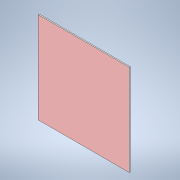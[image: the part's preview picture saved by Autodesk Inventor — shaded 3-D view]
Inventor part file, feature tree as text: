
AUTODESK INVENTOR PART (.ipt)
format: ipt  version: 2022 (Build 260153000, 153)  size: 109,568 bytes
history: native  units: mm
features: extrude x2, sketch x2, other x1
ambient origin geometry x8: Origin, YZ Plane, XZ Plane, XY Plane, X Axis, Y Axis, Z Axis, Center Point
bodies: Body1 (feature_tree)
feature tree (5):
  other  "솔리드1"
  extrude  "돌출1"  Depth=80.0mm
  extrude  "돌출2"  Depth=80.0mm
  sketch  "스케치1"
  sketch  "스케치2"
